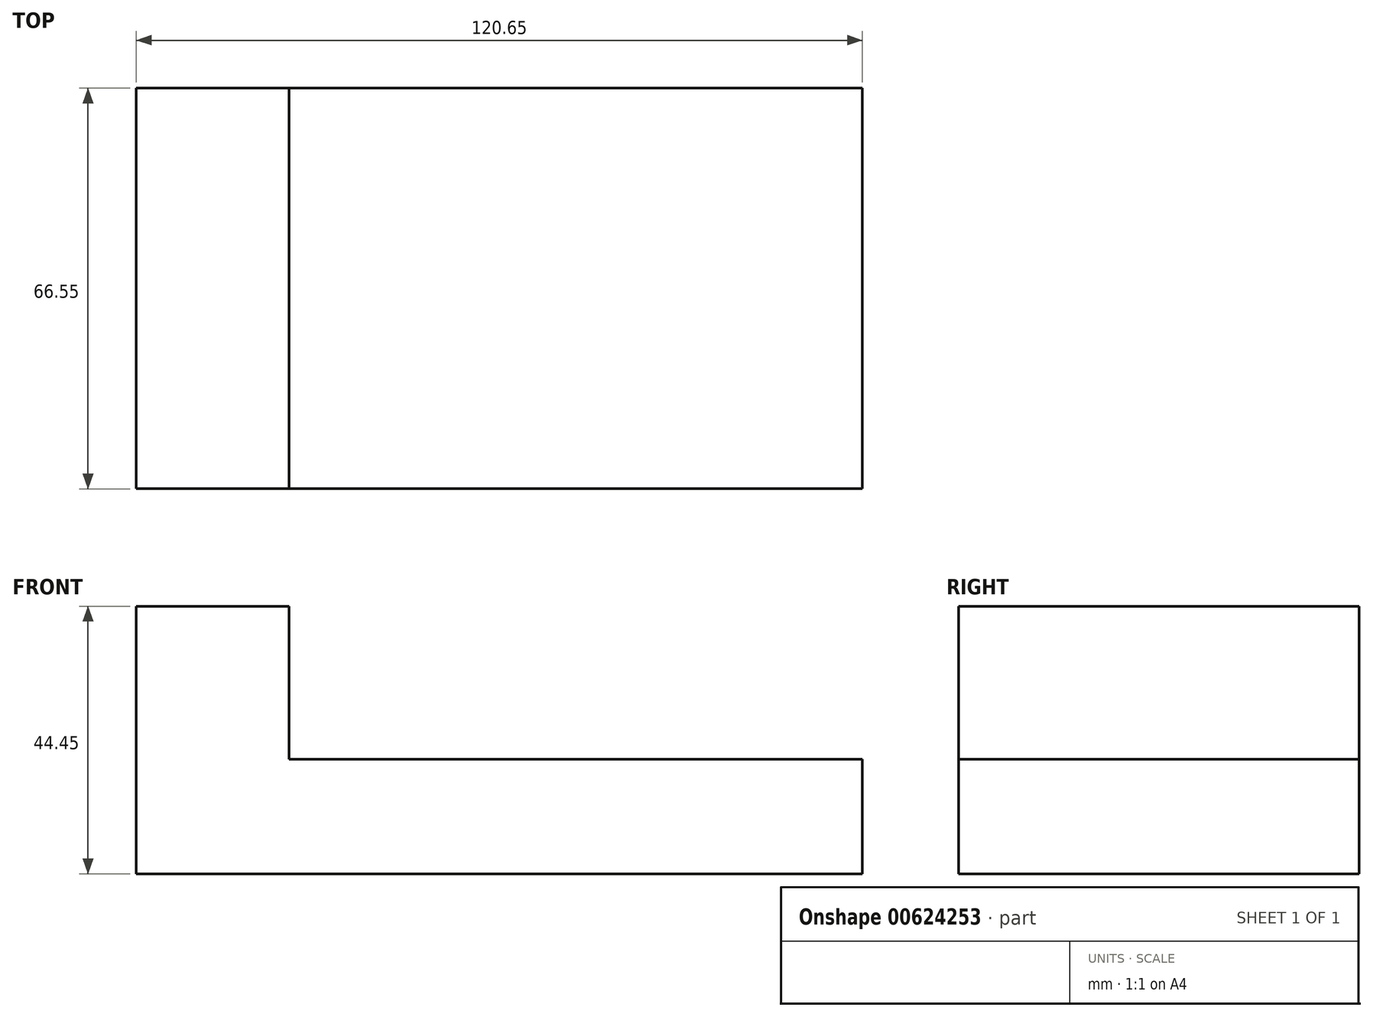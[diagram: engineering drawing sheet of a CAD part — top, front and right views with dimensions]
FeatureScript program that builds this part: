
annotation { "Feature Type Name" : "Feature", "Feature Type Description" : "" }
export const myFeature = defineFeature(function(context is Context, id is Id, definition is map)
    precondition{}
    {
        {
            var Q0;
            Q0=qCreatedBy(makeId("Front.planeOp"),FACE);
            var sketch = newSketch(context, id + "F0", { "sketchPlane" : qUnion([Q0])});
            skLineSegment(sketch, "E0", {"start": v(0, 25.4) * mm, "end": v(25.4, 25.4) * mm});
            skLineSegment(sketch, "E1", {"start": v(25.4, 25.4) * mm, "end": v(25.4, 0) * mm});
            skLineSegment(sketch, "E2", {"start": v(25.4, 0) * mm, "end": v(120.65, 0) * mm});
            skLineSegment(sketch, "E3", {"start": v(120.65, 0) * mm, "end": v(120.65, -19.05) * mm});
            skLineSegment(sketch, "E4", {"start": v(120.65, -19.05) * mm, "end": v(0, -19.05) * mm});
            skLineSegment(sketch, "E5", {"start": v(0, 25.4) * mm, "end": v(0, -19.05) * mm});
            skSolve(sketch);
        }
        {
            var Q0;
            Q0=sQuery(id+"F0.wireOp",EDGE,"E0");
            var Q1;
            Q1=sQuery(id+"F0.wireOp",EDGE,"E5");
            var Q2;
            Q2=sQuery(id+"F0.wireOp",EDGE,"E1");
            var Q3;
            Q3=sQuery(id+"F0.wireOp",EDGE,"E2");
            var Q4;
            Q4=sQuery(id+"F0.wireOp",EDGE,"E4");
            var Q5;
            Q5=sQuery(id+"F0.wireOp",EDGE,"E3");
            extrude(context, id + "F1", {"bodyType" : ToolBodyType.SURFACE, "surfaceEntities" : qUnion([Q0, Q1, Q2, Q3, Q4, Q5]), "depth" : 66.55 * mm, "offsetDistance" : 25.4 * mm});
        }
    });
